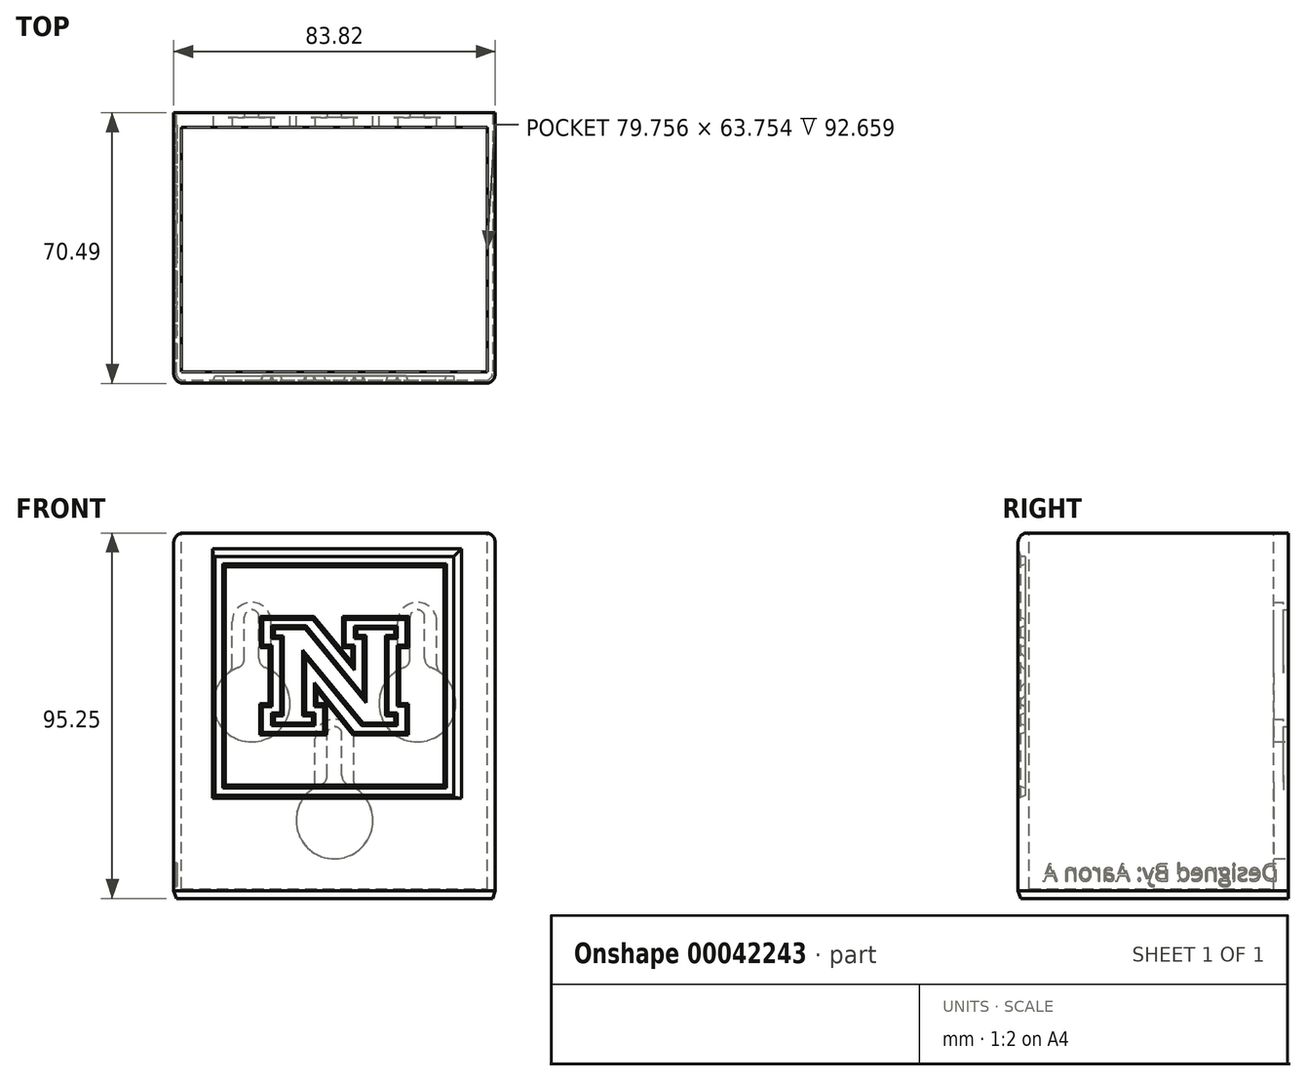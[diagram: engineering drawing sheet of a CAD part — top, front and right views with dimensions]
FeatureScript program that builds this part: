
annotation { "Feature Type Name" : "Feature", "Feature Type Description" : "" }
export const myFeature = defineFeature(function(context is Context, id is Id, definition is map)
    precondition{}
    {
        {
            var Q0;
            Q0=qCreatedBy(makeId("Front.planeOp"),FACE);
            var sketch = newSketch(context, id + "F0", { "sketchPlane" : qUnion([Q0])});
            skLineSegment(sketch, "E0.bottom", {"start": v(0, 0) * mm, "end": v(83.82, 0) * mm});
            skLineSegment(sketch, "E0.top", {"start": v(0, 95.25) * mm, "end": v(83.82, 95.25) * mm});
            skLineSegment(sketch, "E0.left", {"start": v(0, 0) * mm, "end": v(0, 95.25) * mm});
            skLineSegment(sketch, "E0.right", {"start": v(83.82, 0) * mm, "end": v(83.82, 95.25) * mm});
            skLineSegment(sketch, "E1", {"start": v(41.9, 95.25) * mm, "end": v(41.91, 0) * mm});
            skArc(sketch, "E2", {"start": v(18.42, 60.62) * mm, "mid": v(20.32, 40.8) * mm, "end": v(22.23, 60.62) * mm});
            skLineSegment(sketch, "E3", {"start": v(22.23, 60.62) * mm, "end": v(22.23, 73.32) * mm});
            skLineSegment(sketch, "E4", {"start": v(18.42, 60.62) * mm, "end": v(18.42, 73.32) * mm});
            skArc(sketch, "E5", {"start": v(22.23, 73.32) * mm, "mid": v(20.32, 75.22) * mm, "end": v(18.42, 73.32) * mm});
            skArc(sketch, "E6.MirrorCS", {"start": v(65.4, 60.62) * mm, "mid": v(63.5, 40.8) * mm, "end": v(61.6, 60.62) * mm});
            skLineSegment(sketch, "E7.MirrorCS", {"start": v(61.6, 60.62) * mm, "end": v(61.6, 73.32) * mm});
            skLineSegment(sketch, "E8.MirrorCS", {"start": v(65.4, 60.62) * mm, "end": v(65.4, 73.32) * mm});
            skArc(sketch, "E9.MirrorCS", {"start": v(61.6, 73.32) * mm, "mid": v(63.5, 75.22) * mm, "end": v(65.4, 73.32) * mm});
            skArc(sketch, "E10", {"start": v(40, 30.14) * mm, "mid": v(41.91, 10.32) * mm, "end": v(43.82, 30.14) * mm});
            skLineSegment(sketch, "E11", {"start": v(40, 30.14) * mm, "end": v(40, 42.84) * mm});
            skLineSegment(sketch, "E12", {"start": v(43.82, 30.14) * mm, "end": v(43.82, 42.84) * mm});
            skArc(sketch, "E13", {"start": v(43.82, 42.84) * mm, "mid": v(41.91, 44.74) * mm, "end": v(40, 42.84) * mm});
            skSolve(sketch);
        }
        {
            var Q0;
            {var subQ2=sQuery(id+"F0.wireOp",EDGE,"E0.left");Q0=makeQuery(id+"F0.imprint","IMPRINT",FACE,{"disambiguationData":[TD([[makeQuery(id+"F0.imprint","IMPRINT",EDGE,{"derivedFrom":subQ2}),-1.0]])]});}
            var Q1;
            {var subQ2=sQuery(id+"F0.wireOp",EDGE,"E0.right");Q1=makeQuery(id+"F0.imprint","IMPRINT",FACE,{"disambiguationData":[TD([[makeQuery(id+"F0.imprint","IMPRINT",EDGE,{"derivedFrom":subQ2}),1.0]])]});}
            extrude(context, id + "F1", {"entities" : qUnion([Q0, Q1]), "depth" : 1.27 * mm});
        }
        {
            var Q0;
            Q0=makeQuery(id+"F1.opExtrude","CAP_FACE",FACE,{"disambiguationData":[OSD([sQuery(id+"F0.wireOp",EDGE,"E0.bottom"),sQuery(id+"F0.wireOp",EDGE,"E0.top"),sQuery(id+"F0.wireOp",EDGE,"E0.left"),sQuery(id+"F0.wireOp",EDGE,"E0.right"),sQuery(id+"F0.wireOp",EDGE,"E2"),sQuery(id+"F0.wireOp",EDGE,"E3"),sQuery(id+"F0.wireOp",EDGE,"E4"),sQuery(id+"F0.wireOp",EDGE,"E5"),sQuery(id+"F0.wireOp",EDGE,"E6.MirrorCS"),sQuery(id+"F0.wireOp",EDGE,"E7.MirrorCS"),sQuery(id+"F0.wireOp",EDGE,"E8.MirrorCS"),sQuery(id+"F0.wireOp",EDGE,"E9.MirrorCS")])],"isStart":false});
            var sketch = newSketch(context, id + "F2", { "sketchPlane" : qUnion([Q0])});
            skArc(sketch, "E14", {"start": v(15.24, 59.41) * mm, "mid": v(20.32, 40.8) * mm, "end": v(25.4, 59.41) * mm});
            skLineSegment(sketch, "E15", {"start": v(41.9, 95.25) * mm, "end": v(41.9, 0) * mm});
            skLineSegment(sketch, "E16", {"start": v(25.4, 59.41) * mm, "end": v(25.4, 72.11) * mm});
            skLineSegment(sketch, "E17", {"start": v(15.24, 59.41) * mm, "end": v(15.24, 72.11) * mm});
            skArc(sketch, "E18", {"start": v(25.4, 72.11) * mm, "mid": v(20.32, 77.2) * mm, "end": v(15.24, 72.11) * mm});
            skLineSegment(sketch, "E19.MirrorCS", {"start": v(68.58, 59.41) * mm, "end": v(68.58, 72.11) * mm});
            skArc(sketch, "E20.MirrorCS", {"start": v(58.42, 72.11) * mm, "mid": v(63.5, 77.2) * mm, "end": v(68.58, 72.11) * mm});
            skLineSegment(sketch, "E21.MirrorCS", {"start": v(58.42, 59.41) * mm, "end": v(58.42, 72.11) * mm});
            skArc(sketch, "E22.MirrorCS", {"start": v(68.58, 59.41) * mm, "mid": v(63.5, 40.8) * mm, "end": v(58.42, 59.41) * mm});
            skLineSegment(sketch, "E23.MirrorCS", {"start": v(36.83, 28.93) * mm, "end": v(36.83, 41.63) * mm});
            skLineSegment(sketch, "E24.MirrorCS", {"start": v(46.99, 28.93) * mm, "end": v(46.99, 41.63) * mm});
            skArc(sketch, "E25.MirrorCS", {"start": v(36.83, 41.63) * mm, "mid": v(41.9, 46.71) * mm, "end": v(46.99, 41.63) * mm});
            skSolve(sketch);
        }
        {
            var Q0;
            Q0=makeQuery(id+"F2.imprint","IMPRINT",FACE,{"disambiguationData":[TD([[makeQuery(id+"F2.imprint","IMPRINT",EDGE,{"derivedFrom":sQuery(id+"F2.wireOp",EDGE,"E14")}),-1.0]])]});
            var Q1;
            {var subQ2=sQuery(id+"F2.wireOp",EDGE,"E15");Q1=makeQuery(id+"F2.imprint","IMPRINT",FACE,{"disambiguationData":[TD([[makeQuery(id+"F2.imprint","IMPRINT",EDGE,{"derivedFrom":subQ2}),1.0]])]});}
            extrude(context, id + "F3", {"entities" : qUnion([Q0, Q1]), "operationType" : NewBodyOperationType.ADD, "depth" : 5.08 * mm});
        }
        {
            var Q0;
            Q0=makeQuery(id+"F3.opExtrude","CAP_FACE",FACE,{"disambiguationData":[OSD([sQuery(id+"F0.wireOp",EDGE,"E0.bottom"),sQuery(id+"F0.wireOp",EDGE,"E0.top"),sQuery(id+"F0.wireOp",EDGE,"E0.left"),sQuery(id+"F0.wireOp",EDGE,"E0.right"),sQuery(id+"F2.wireOp",EDGE,"E14"),sQuery(id+"F2.wireOp",EDGE,"E16"),sQuery(id+"F2.wireOp",EDGE,"E17"),sQuery(id+"F2.wireOp",EDGE,"E18"),sQuery(id+"F2.wireOp",EDGE,"E19.MirrorCS"),sQuery(id+"F2.wireOp",EDGE,"E20.MirrorCS"),sQuery(id+"F2.wireOp",EDGE,"E21.MirrorCS"),sQuery(id+"F2.wireOp",EDGE,"E22.MirrorCS")])],"isStart":false});
            var sketch = newSketch(context, id + "F4", { "sketchPlane" : qUnion([Q0])});
            skLineSegment(sketch, "E26.bottom", {"start": v(0, 0) * mm, "end": v(83.82, 0) * mm});
            skLineSegment(sketch, "E26.top", {"start": v(0, 95.25) * mm, "end": v(83.82, 95.25) * mm});
            skLineSegment(sketch, "E26.left", {"start": v(0, 0) * mm, "end": v(0, 95.25) * mm});
            skLineSegment(sketch, "E26.right", {"start": v(83.82, 0) * mm, "end": v(83.82, 95.25) * mm});
            skSolve(sketch);
        }
        {
            var Q0;
            Q0 = qSketchRegion(id + "F4", true);
            extrude(context, id + "F5", {"entities" : qUnion([Q0]), "operationType" : NewBodyOperationType.ADD, "depth" : 64.13 * mm});
        }
        {
            var Q0;
            {var subQ0=sQuery(id+"F0.wireOp",EDGE,"E0.top");Q0=makeQuery(id+"F5.boolean.opBoolean","MERGE",FACE,{"derivedFrom":[makeQuery(id+"F3.boolean.opBoolean","MERGE",FACE,{"derivedFrom":[makeQuery(id+"F1.opExtrude","SWEPT_FACE",FACE,{"disambiguationData":[OSD([subQ0])]}),makeQuery(id+"F3.opExtrude","SWEPT_FACE",FACE,{"disambiguationData":[OSD([subQ0])]})]}),makeQuery(id+"F5.opExtrude","SWEPT_FACE",FACE,{"disambiguationData":[OSD([sQuery(id+"F4.wireOp",EDGE,"E26.top")])]})]});}
            var sketch = newSketch(context, id + "F6", { "sketchPlane" : qUnion([Q0])});
            skLineSegment(sketch, "E27.bottom", {"start": v(2.03, -67.56) * mm, "end": v(81.79, -67.56) * mm});
            skLineSegment(sketch, "E27.top", {"start": v(2.03, -3.81) * mm, "end": v(81.79, -3.81) * mm});
            skLineSegment(sketch, "E27.left", {"start": v(2.03, -67.56) * mm, "end": v(2.03, -3.81) * mm});
            skLineSegment(sketch, "E27.right", {"start": v(81.79, -67.56) * mm, "end": v(81.79, -3.81) * mm});
            skSolve(sketch);
        }
        {
            var Q0;
            Q0=makeQuery(id+"F6.imprint","IMPRINT",FACE,{"disambiguationData":[TD([[makeQuery(id+"F6.imprint","IMPRINT",EDGE,{"derivedFrom":sQuery(id+"F6.wireOp",EDGE,"E27.bottom")}),1.0]])]});
            extrude(context, id + "F7", {"entities" : qUnion([Q0]), "operationType" : NewBodyOperationType.REMOVE, "oppositeDirection" : true, "depth" : 92.7 * mm});
        }
        {
            var Q0;
            Q0=makeQuery(id+"F1.opExtrude","SWEPT_EDGE",EDGE,{"disambiguationData":[OSD([sQuery(id+"F0.wireOp",EDGE,"E6.MirrorCS"),sQuery(id+"F0.wireOp",EDGE,"E8.MirrorCS")])]});
            var Q1;
            Q1=makeQuery(id+"F3.opExtrude","SWEPT_EDGE",EDGE,{"disambiguationData":[OSD([sQuery(id+"F0.wireOp",EDGE,"E6.MirrorCS"),sQuery(id+"F2.wireOp",EDGE,"E19.MirrorCS"),sQuery(id+"F2.wireOp",EDGE,"E22.MirrorCS")])]});
            var Q2;
            Q2=makeQuery(id+"F3.opExtrude","SWEPT_EDGE",EDGE,{"disambiguationData":[OSD([sQuery(id+"F0.wireOp",EDGE,"E6.MirrorCS"),sQuery(id+"F2.wireOp",EDGE,"E21.MirrorCS"),sQuery(id+"F2.wireOp",EDGE,"E22.MirrorCS")])]});
            var Q3;
            Q3=makeQuery(id+"F1.opExtrude","SWEPT_EDGE",EDGE,{"disambiguationData":[OSD([sQuery(id+"F0.wireOp",EDGE,"E6.MirrorCS"),sQuery(id+"F0.wireOp",EDGE,"E7.MirrorCS")])]});
            fillet(context, id + "F8", {"entities" : qUnion([Q0, Q1, Q2, Q3]), "radius" : 2.54 * mm, "tangentPropagation" : true, "allowEdgeOverflow" : false});
        }
        {
            var Q0;
            Q0=makeQuery(id+"F3.opExtrude","SWEPT_EDGE",EDGE,{"disambiguationData":[OSD([sQuery(id+"F0.wireOp",EDGE,"E2"),sQuery(id+"F2.wireOp",EDGE,"E14"),sQuery(id+"F2.wireOp",EDGE,"E16")])]});
            var Q1;
            Q1=makeQuery(id+"F1.opExtrude","SWEPT_EDGE",EDGE,{"disambiguationData":[OSD([sQuery(id+"F0.wireOp",EDGE,"E2"),sQuery(id+"F0.wireOp",EDGE,"E3")])]});
            var Q2;
            Q2=makeQuery(id+"F1.opExtrude","SWEPT_EDGE",EDGE,{"disambiguationData":[OSD([sQuery(id+"F0.wireOp",EDGE,"E2"),sQuery(id+"F0.wireOp",EDGE,"E4")])]});
            var Q3;
            Q3=makeQuery(id+"F3.opExtrude","SWEPT_EDGE",EDGE,{"disambiguationData":[OSD([sQuery(id+"F0.wireOp",EDGE,"E2"),sQuery(id+"F2.wireOp",EDGE,"E14"),sQuery(id+"F2.wireOp",EDGE,"E17")])]});
            var Q4;
            Q4=makeQuery(id+"F3.opExtrude","SWEPT_EDGE",EDGE,{"disambiguationData":[OSD([sQuery(id+"F0.wireOp",EDGE,"E10"),sQuery(id+"F2.wireOp",EDGE,"E23.MirrorCS")])]});
            var Q5;
            Q5=makeQuery(id+"F1.opExtrude","SWEPT_EDGE",EDGE,{"disambiguationData":[OSD([sQuery(id+"F0.wireOp",EDGE,"E10"),sQuery(id+"F0.wireOp",EDGE,"E11")])]});
            var Q6;
            Q6=makeQuery(id+"F1.opExtrude","SWEPT_EDGE",EDGE,{"disambiguationData":[OSD([sQuery(id+"F0.wireOp",EDGE,"E10"),sQuery(id+"F0.wireOp",EDGE,"E12")])]});
            var Q7;
            Q7=makeQuery(id+"F3.opExtrude","SWEPT_EDGE",EDGE,{"disambiguationData":[OSD([sQuery(id+"F0.wireOp",EDGE,"E10"),sQuery(id+"F2.wireOp",EDGE,"E24.MirrorCS")])]});
            fillet(context, id + "F9", {"entities" : qUnion([Q0, Q1, Q2, Q3, Q4, Q5, Q6, Q7]), "radius" : 2.54 * mm, "tangentPropagation" : true, "allowEdgeOverflow" : false});
        }
        {
            var Q0;
            {var subQ0=sQuery(id+"F0.wireOp",EDGE,"E0.top");var subQ1=sQuery(id+"F0.wireOp",EDGE,"E0.left");Q0=makeQuery(id+"F5.boolean.opBoolean","MERGE",EDGE,{"derivedFrom":[makeQuery(id+"F3.boolean.opBoolean","MERGE",EDGE,{"derivedFrom":[makeQuery(id+"F1.opExtrude","SWEPT_EDGE",EDGE,{"disambiguationData":[OSD([subQ0,subQ1])]}),makeQuery(id+"F3.opExtrude","SWEPT_EDGE",EDGE,{"disambiguationData":[OSD([subQ0,subQ1])]})]}),makeQuery(id+"F5.opExtrude","SWEPT_EDGE",EDGE,{"disambiguationData":[OSD([sQuery(id+"F4.wireOp",EDGE,"E26.top"),sQuery(id+"F4.wireOp",EDGE,"E26.left")])]})]});}
            var Q1;
            Q1=makeQuery(id+"F5.opExtrude","CAP_EDGE",EDGE,{"disambiguationData":[OSD([sQuery(id+"F4.wireOp",EDGE,"E26.top")])],"isStart":false});
            var Q2;
            {var subQ0=sQuery(id+"F0.wireOp",EDGE,"E0.top");var subQ1=sQuery(id+"F0.wireOp",EDGE,"E0.right");Q2=makeQuery(id+"F5.boolean.opBoolean","MERGE",EDGE,{"derivedFrom":[makeQuery(id+"F3.boolean.opBoolean","MERGE",EDGE,{"derivedFrom":[makeQuery(id+"F1.opExtrude","SWEPT_EDGE",EDGE,{"disambiguationData":[OSD([subQ0,subQ1])]}),makeQuery(id+"F3.opExtrude","SWEPT_EDGE",EDGE,{"disambiguationData":[OSD([subQ0,subQ1])]})]}),makeQuery(id+"F5.opExtrude","SWEPT_EDGE",EDGE,{"disambiguationData":[OSD([sQuery(id+"F4.wireOp",EDGE,"E26.top"),sQuery(id+"F4.wireOp",EDGE,"E26.right")])]})]});}
            var Q3;
            Q3=makeQuery(id+"F5.opExtrude","CAP_EDGE",EDGE,{"disambiguationData":[OSD([sQuery(id+"F4.wireOp",EDGE,"E26.right")])],"isStart":false});
            var Q4;
            Q4=makeQuery(id+"F5.opExtrude","CAP_EDGE",EDGE,{"disambiguationData":[OSD([sQuery(id+"F4.wireOp",EDGE,"E26.left")])],"isStart":false});
            fillet(context, id + "F10", {"entities" : qUnion([Q0, Q1, Q2, Q3, Q4]), "radius" : 2.54 * mm, "tangentPropagation" : true, "allowEdgeOverflow" : false});
        }
        {
            var Q0;
            {var subQ0=sQuery(id+"F0.wireOp",EDGE,"E0.left");Q0=makeQuery(id+"F5.boolean.opBoolean","MERGE",FACE,{"derivedFrom":[makeQuery(id+"F3.boolean.opBoolean","MERGE",FACE,{"derivedFrom":[makeQuery(id+"F1.opExtrude","SWEPT_FACE",FACE,{"disambiguationData":[OSD([subQ0])]}),makeQuery(id+"F3.opExtrude","SWEPT_FACE",FACE,{"disambiguationData":[OSD([subQ0])]})]}),makeQuery(id+"F5.opExtrude","SWEPT_FACE",FACE,{"disambiguationData":[OSD([sQuery(id+"F4.wireOp",EDGE,"E26.left")])]})]});}
            var sketch = newSketch(context, id + "F11", { "sketchPlane" : qUnion([Q0])});
            skText(sketch, "E28", { "text": "Designed By: Aaron A", "fontName": "OpenSans-Regular.ttf"});
            const initialGuessF11  = {"E28": [0.00254, 0.00457, 1, 0, 0.00443]};
            skSetInitialGuess(sketch, initialGuessF11);
            skSolve(sketch);
        }
        {
            var Q0;
            Q0 = qSketchRegion(id + "F11", true);
            var Q1;
            Q1 = qSketchRegion(id + "F13", true);
            extrude(context, id + "F12", {"entities" : qUnion([Q0, Q1]), "operationType" : NewBodyOperationType.REMOVE, "oppositeDirection" : true, "depth" : 1.65 * mm - .8 * mm});
        }
        {
            var Q0;
            Q0=makeQuery(id+"F5.opExtrude","CAP_FACE",FACE,{"disambiguationData":[OSD([sQuery(id+"F4.wireOp",EDGE,"E26.bottom"),sQuery(id+"F4.wireOp",EDGE,"E26.top"),sQuery(id+"F4.wireOp",EDGE,"E26.left"),sQuery(id+"F4.wireOp",EDGE,"E26.right")])],"isStart":false});
            var sketch = newSketch(context, id + "F13", { "sketchPlane" : qUnion([Q0])});
            skLineSegment(sketch, "E29", {"start": v(23.24, 72.7) * mm, "end": v(23.24, 66.03) * mm});
            skLineSegment(sketch, "E30", {"start": v(23.24, 66.03) * mm, "end": v(25.6, 66.03) * mm});
            skLineSegment(sketch, "E31", {"start": v(25.6, 66.03) * mm, "end": v(25.6, 49.95) * mm});
            skLineSegment(sketch, "E32", {"start": v(25.6, 49.95) * mm, "end": v(23.18, 49.95) * mm});
            skLineSegment(sketch, "E33", {"start": v(23.18, 49.95) * mm, "end": v(23.18, 43.35) * mm});
            skLineSegment(sketch, "E34", {"start": v(23.18, 43.35) * mm, "end": v(39.06, 43.35) * mm});
            skLineSegment(sketch, "E35", {"start": v(39.06, 43.35) * mm, "end": v(39.06, 49.95) * mm});
            skLineSegment(sketch, "E36", {"start": v(39.06, 49.95) * mm, "end": v(36.57, 49.95) * mm});
            skLineSegment(sketch, "E37", {"start": v(36.57, 49.95) * mm, "end": v(36.57, 56.3) * mm});
            skLineSegment(sketch, "E38", {"start": v(36.57, 56.3) * mm, "end": v(47.03, 43.35) * mm});
            skLineSegment(sketch, "E39", {"start": v(47.03, 43.35) * mm, "end": v(60.5, 43.35) * mm});
            skLineSegment(sketch, "E40", {"start": v(60.5, 43.35) * mm, "end": v(60.5, 50.02) * mm});
            skLineSegment(sketch, "E41", {"start": v(60.5, 50.02) * mm, "end": v(58.17, 50.02) * mm});
            skLineSegment(sketch, "E42", {"start": v(58.17, 50.02) * mm, "end": v(58.17, 66.1) * mm});
            skLineSegment(sketch, "E43", {"start": v(58.17, 66.1) * mm, "end": v(60.52, 66.1) * mm});
            skLineSegment(sketch, "E44", {"start": v(60.52, 66.1) * mm, "end": v(60.52, 72.7) * mm});
            skLineSegment(sketch, "E45", {"start": v(60.52, 72.7) * mm, "end": v(44.7, 72.7) * mm});
            skLineSegment(sketch, "E46", {"start": v(44.7, 72.7) * mm, "end": v(44.7, 66.1) * mm});
            skLineSegment(sketch, "E47", {"start": v(44.7, 66.1) * mm, "end": v(47.16, 66.1) * mm});
            skLineSegment(sketch, "E48", {"start": v(47.16, 66.1) * mm, "end": v(47.16, 59.43) * mm});
            skLineSegment(sketch, "E49", {"start": v(47.16, 59.43) * mm, "end": v(36.25, 72.7) * mm});
            skLineSegment(sketch, "E50", {"start": v(36.25, 72.7) * mm, "end": v(23.24, 72.7) * mm});
            skLineSegment(sketch, "E51", {"start": v(25.5, 71.06) * mm, "end": v(25.5, 67.66) * mm});
            skLineSegment(sketch, "E52", {"start": v(25.5, 67.66) * mm, "end": v(27.85, 67.66) * mm});
            skLineSegment(sketch, "E53", {"start": v(27.85, 67.66) * mm, "end": v(27.85, 48.32) * mm});
            skLineSegment(sketch, "E54", {"start": v(27.85, 48.32) * mm, "end": v(25.5, 48.32) * mm});
            skLineSegment(sketch, "E55", {"start": v(25.5, 48.32) * mm, "end": v(25.5, 44.99) * mm});
            skLineSegment(sketch, "E56", {"start": v(25.5, 44.99) * mm, "end": v(36.86, 44.99) * mm});
            skLineSegment(sketch, "E57", {"start": v(36.86, 44.99) * mm, "end": v(36.86, 48.32) * mm});
            skLineSegment(sketch, "E58", {"start": v(36.86, 48.32) * mm, "end": v(34.38, 48.32) * mm});
            skLineSegment(sketch, "E59", {"start": v(34.38, 48.32) * mm, "end": v(34.38, 62.63) * mm});
            skLineSegment(sketch, "E60", {"start": v(34.38, 62.63) * mm, "end": v(48.95, 44.99) * mm});
            skLineSegment(sketch, "E61", {"start": v(48.95, 44.99) * mm, "end": v(58.3, 44.99) * mm});
            skLineSegment(sketch, "E62", {"start": v(58.3, 44.99) * mm, "end": v(58.3, 48.32) * mm});
            skLineSegment(sketch, "E63", {"start": v(58.3, 48.32) * mm, "end": v(55.88, 48.32) * mm});
            skLineSegment(sketch, "E64", {"start": v(55.88, 48.32) * mm, "end": v(55.88, 67.73) * mm});
            skLineSegment(sketch, "E65", {"start": v(55.88, 67.73) * mm, "end": v(58.3, 67.73) * mm});
            skLineSegment(sketch, "E66", {"start": v(58.3, 67.73) * mm, "end": v(58.3, 71) * mm});
            skLineSegment(sketch, "E67", {"start": v(58.3, 71) * mm, "end": v(47, 71) * mm});
            skLineSegment(sketch, "E68", {"start": v(47, 71) * mm, "end": v(47, 67.73) * mm});
            skLineSegment(sketch, "E69", {"start": v(47, 67.73) * mm, "end": v(49.35, 67.73) * mm});
            skLineSegment(sketch, "E70", {"start": v(49.35, 67.73) * mm, "end": v(49.35, 53.1) * mm});
            skLineSegment(sketch, "E71", {"start": v(49.35, 53.1) * mm, "end": v(34.57, 71.06) * mm});
            skLineSegment(sketch, "E72", {"start": v(34.57, 71.06) * mm, "end": v(25.5, 71.06) * mm});
            skLineSegment(sketch, "E73.bottom", {"start": v(10.8, 89.09) * mm, "end": v(73.02, 89.09) * mm});
            skLineSegment(sketch, "E73.top", {"start": v(10.8, 26.86) * mm, "end": v(73.02, 26.86) * mm});
            skLineSegment(sketch, "E74.bottom", {"start": v(12.7, 87.18) * mm, "end": v(71.12, 87.18) * mm});
            skLineSegment(sketch, "E74.top", {"start": v(12.7, 28.76) * mm, "end": v(71.12, 28.76) * mm});
            skLineSegment(sketch, "E74.left", {"start": v(12.7, 87.18) * mm, "end": v(12.7, 28.76) * mm});
            skLineSegment(sketch, "E74.right", {"start": v(71.12, 87.18) * mm, "end": v(71.12, 28.76) * mm});
            skLineSegment(sketch, "E75.left", {"start": v(10.8, 89.09) * mm, "end": v(10.8, 26.86) * mm});
            skLineSegment(sketch, "E75.right", {"start": v(73.02, 89.09) * mm, "end": v(73.02, 26.86) * mm});
            skSolve(sketch);
        }
        {
            var Q0;
            Q0 = qSketchRegion(id + "F13", true);
            var Q1;
            Q1=makeQuery(id+"F13.imprint","IMPRINT",FACE,{"disambiguationData":[TD([[makeQuery(id+"F13.imprint","IMPRINT",EDGE,{"derivedFrom":sQuery(id+"F13.wireOp",EDGE,"E29")}),1.0]])]});
            extrude(context, id + "F14", {"entities" : qUnion([Q0, Q1]), "operationType" : NewBodyOperationType.REMOVE, "oppositeDirection" : true, "depth" : 1.9 * mm});
        }
        {
            var Q0;
            Q0=makeQuery(id+"F14.boolean.opBoolean","SPLIT",FACE,{"disambiguationData":[TD([makeQuery(id+"F14.opExtrude","SWEPT_FACE",FACE,{"disambiguationData":[OSD([sQuery(id+"F13.wireOp",EDGE,"E51")])]})])],"derivedFrom":makeQuery(id+"F5.opExtrude","CAP_FACE",FACE,{"disambiguationData":[OSD([sQuery(id+"F4.wireOp",EDGE,"E26.bottom"),sQuery(id+"F4.wireOp",EDGE,"E26.top"),sQuery(id+"F4.wireOp",EDGE,"E26.left"),sQuery(id+"F4.wireOp",EDGE,"E26.right")])],"isStart":false})});
            chamfer(context, id + "F15", {"entities" : qUnion([Q0]), "chamferType" : ChamferType.OFFSET_ANGLE, "width" : 2.03 * mm, "oppositeDirection" : true, "angle" : 20 * degree, "tangentPropagation" : true});
        }
        {
            var Q0;
            Q0=makeQuery(id+"F14.boolean.opBoolean","SPLIT",FACE,{"disambiguationData":[TD([makeQuery(id+"F14.opExtrude","SWEPT_FACE",FACE,{"disambiguationData":[OSD([sQuery(id+"F13.wireOp",EDGE,"E29")])]})])],"derivedFrom":makeQuery(id+"F5.opExtrude","CAP_FACE",FACE,{"disambiguationData":[OSD([sQuery(id+"F4.wireOp",EDGE,"E26.bottom"),sQuery(id+"F4.wireOp",EDGE,"E26.top"),sQuery(id+"F4.wireOp",EDGE,"E26.left"),sQuery(id+"F4.wireOp",EDGE,"E26.right")])],"isStart":false})});
            var Q1;
            {var subQ0=sQuery(id+"F4.wireOp",EDGE,"E26.bottom");var subQ1=sQuery(id+"F4.wireOp",EDGE,"E26.right");var subQ2=sQuery(id+"F4.wireOp",EDGE,"E26.top");var subQ5=sQuery(id+"F0.wireOp",EDGE,"E0.bottom");var subQ6=sQuery(id+"F4.wireOp",EDGE,"E26.left");Q1=makeQuery(id+"F14.boolean.opBoolean","SPLIT",FACE,{"disambiguationData":[TD([makeQuery(id+"F1.opExtrude","SWEPT_FACE",FACE,{"disambiguationData":[OSD([subQ5])]})])],"derivedFrom":makeQuery(id+"F5.opExtrude","CAP_FACE",FACE,{"disambiguationData":[OSD([subQ0,subQ2,subQ6,subQ1])],"isStart":false})});}
            chamfer(context, id + "F16", {"entities" : qUnion([Q0, Q1]), "chamferType" : ChamferType.OFFSET_ANGLE, "width" : 2.03 * mm, "oppositeDirection" : false, "angle" : 20 * degree, "tangentPropagation" : true});
        }
    });
